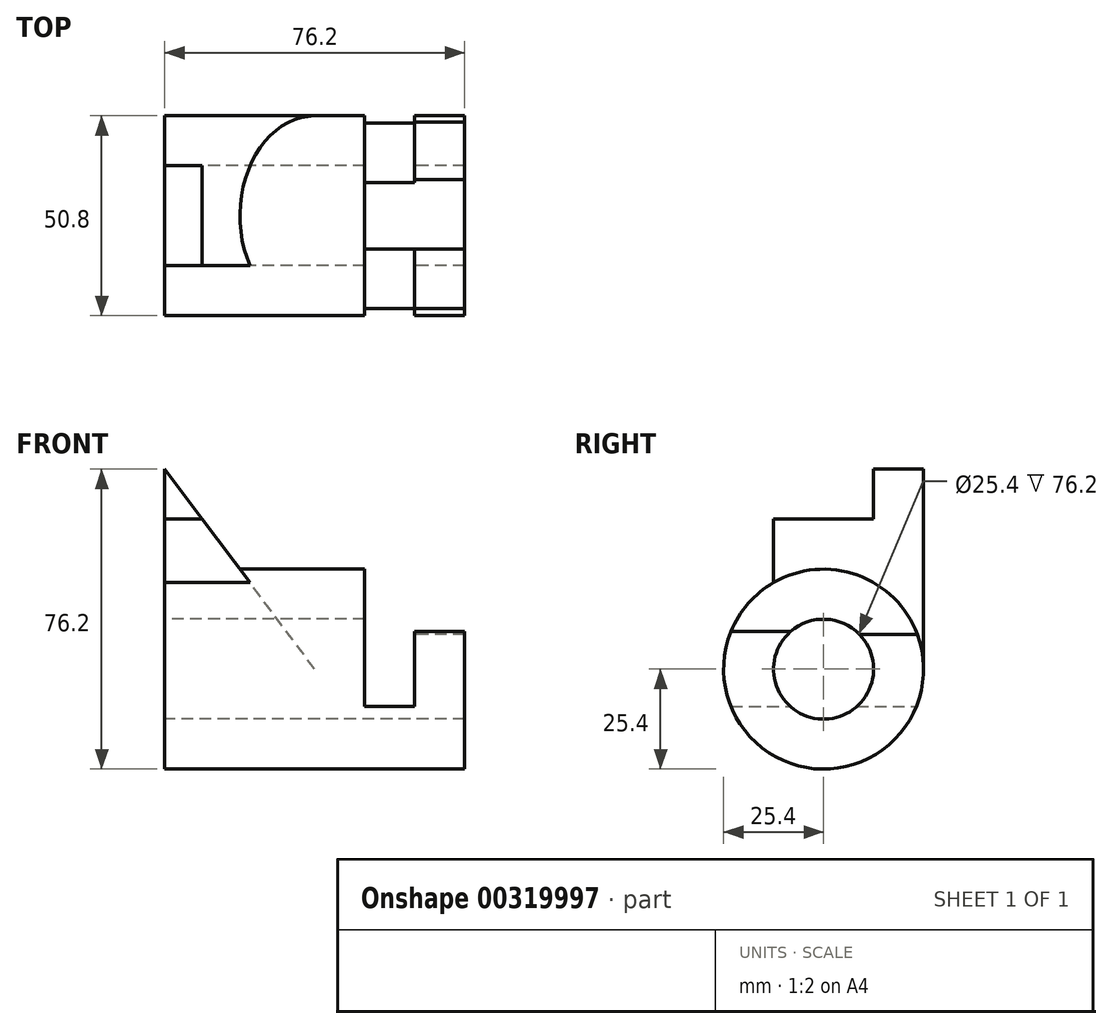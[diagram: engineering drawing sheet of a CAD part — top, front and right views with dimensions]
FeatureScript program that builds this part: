
annotation { "Feature Type Name" : "Feature", "Feature Type Description" : "" }
export const myFeature = defineFeature(function(context is Context, id is Id, definition is map)
    precondition{}
    {
        {
            var Q0;
            Q0=qCreatedBy(makeId("Right.planeOp"),FACE);
            var sketch = newSketch(context, id + "F0", { "sketchPlane" : qUnion([Q0])});
            skCircle(sketch, "E0", {"center": v(0, 0) * mm, "radius": 25.4 * mm});
            skCircle(sketch, "E1", {"center": v(0, 0) * mm, "radius": 12.7 * mm});
            skSolve(sketch);
        }
        {
            var Q0;
            Q0 = qSketchRegion(id + "F0", true);
            extrude(context, id + "F1", {"entities" : qUnion([Q0]), "depth" : 50.8 * mm});
        }
        {
            var Q0;
            Q0=makeQuery(id+"F1.opExtrude","CAP_FACE",FACE,{"disambiguationData":[OSD([sQuery(id+"F0.wireOp",EDGE,"E0"),sQuery(id+"F0.wireOp",EDGE,"E1")])],"isStart":false});
            var sketch = newSketch(context, id + "F2", { "sketchPlane" : qUnion([Q0])});
            skLineSegment(sketch, "E2", {"start": v(-23.55, -9.53) * mm, "end": v(-8.4, -9.53) * mm});
            skLineSegment(sketch, "E3", {"start": v(8.4, -9.53) * mm, "end": v(23.55, -9.53) * mm});
            skArc(sketch, "E4", {"start": v(-8.4, -9.53) * mm, "mid": v(0, -12.7) * mm, "end": v(8.4, -9.53) * mm});
            skArc(sketch, "E5", {"start": v(-23.55, -9.53) * mm, "mid": v(0, -25.4) * mm, "end": v(23.55, -9.52) * mm});
            skSolve(sketch);
        }
        {
            var Q0;
            Q0 = qSketchRegion(id + "F2", true);
            extrude(context, id + "F3", {"entities" : qUnion([Q0]), "operationType" : NewBodyOperationType.ADD, "depth" : 12.7 * mm});
        }
        {
            var Q0;
            Q0=makeQuery(id+"F3.opExtrude","CAP_FACE",FACE,{"disambiguationData":[OSD([sQuery(id+"F2.wireOp",EDGE,"E2"),sQuery(id+"F2.wireOp",EDGE,"E3"),sQuery(id+"F2.wireOp",EDGE,"E4"),sQuery(id+"F2.wireOp",EDGE,"E5")])],"isStart":false});
            var sketch = newSketch(context, id + "F4", { "sketchPlane" : qUnion([Q0])});
            skArc(sketch, "E6", {"start": v(-23.55, 9.52) * mm, "mid": v(-0.39, -25.4) * mm, "end": v(23.83, 8.8) * mm});
            skArc(sketch, "E7", {"start": v(-8.4, 9.53) * mm, "mid": v(-0.52, -12.69) * mm, "end": v(9.15, 8.8) * mm});
            skLineSegment(sketch, "E8", {"start": v(-23.55, 9.53) * mm, "end": v(-8.4, 9.53) * mm});
            skLineSegment(sketch, "E9", {"start": v(9.15, 8.8) * mm, "end": v(23.83, 8.8) * mm});
            skSolve(sketch);
        }
        {
            var Q0;
            Q0 = qSketchRegion(id + "F4", true);
            extrude(context, id + "F5", {"entities" : qUnion([Q0]), "operationType" : NewBodyOperationType.ADD, "depth" : 12.7 * mm});
        }
        {
            var Q0;
            Q0=qCreatedBy(makeId("Front.planeOp"),FACE);
            cPlane(context, id + "F6", {"entities" : qUnion([Q0]), "cplaneType" : CPlaneType.OFFSET, "offset" : 6.35 * mm, "oppositeDirection" : true, "width" : 152.4 * mm, "height" : 152.4 * mm});
        }
        {
            var Q0;
            Q0=qCreatedBy(id+"F6.planeOp",FACE);
            var sketch = newSketch(context, id + "F7", { "sketchPlane" : qUnion([Q0])});
            skLineSegment(sketch, "E10", {"start": v(0, 0) * mm, "end": v(38.1, 0) * mm});
            skLineSegment(sketch, "E11", {"start": v(38.1, 0) * mm, "end": v(0, 50.8) * mm});
            skLineSegment(sketch, "E12", {"start": v(0, 50.8) * mm, "end": v(0, 0) * mm});
            skSolve(sketch);
        }
        {
            var Q0;
            Q0 = qSketchRegion(id + "F7", true);
            extrude(context, id + "F8", {"entities" : qUnion([Q0]), "operationType" : NewBodyOperationType.ADD, "endBound" : BoundingType.SYMMETRIC, "oppositeDirection" : true, "depth" : 38.1 * mm});
        }
        {
            var Q0;
            Q0=makeQuery(id+"F8.boolean.opBoolean","MERGE",FACE,{"derivedFrom":[makeQuery(id+"F1.opExtrude","CAP_FACE",FACE,{"disambiguationData":[OSD([sQuery(id+"F0.wireOp",EDGE,"E0"),sQuery(id+"F0.wireOp",EDGE,"E1")])],"isStart":true}),makeQuery(id+"F8.opExtrude","SWEPT_FACE",FACE,{"disambiguationData":[OSD([sQuery(id+"F7.wireOp",EDGE,"E12")])]})]});
            var sketch = newSketch(context, id + "F9", { "sketchPlane" : qUnion([Q0])});
            skLineSegment(sketch, "E13.0", {"start": v(-12.7, 0) * mm, "end": v(12.7, 0) * mm});
            skArc(sketch, "E14", {"start": v(12.7, 0) * mm, "mid": v(0, 12.7) * mm, "end": v(-12.7, 0) * mm});
            skSolve(sketch);
        }
        {
            var Q0;
            Q0 = qSketchRegion(id + "F9", true);
            extrude(context, id + "F10", {"entities" : qUnion([Q0]), "operationType" : NewBodyOperationType.REMOVE, "oppositeDirection" : true, "depth" : 38.1 * mm});
        }
        {
            var Q0;
            Q0=qCreatedBy(makeId("Right.planeOp"),FACE);
            var sketch = newSketch(context, id + "F11", { "sketchPlane" : qUnion([Q0])});
            skLineSegment(sketch, "E15.bottom", {"start": v(-12.7, 38.1) * mm, "end": v(12.7, 38.1) * mm});
            skLineSegment(sketch, "E15.top", {"start": v(-12.7, 50.8) * mm, "end": v(12.7, 50.8) * mm});
            skLineSegment(sketch, "E15.left", {"start": v(-12.7, 38.1) * mm, "end": v(-12.7, 50.8) * mm});
            skLineSegment(sketch, "E15.right", {"start": v(12.7, 38.1) * mm, "end": v(12.7, 50.8) * mm});
            skSolve(sketch);
        }
        {
            var Q0;
            Q0 = qSketchRegion(id + "F11", true);
            extrude(context, id + "F12", {"entities" : qUnion([Q0]), "operationType" : NewBodyOperationType.REMOVE, "depth" : 12.7 * mm});
        }
    });
